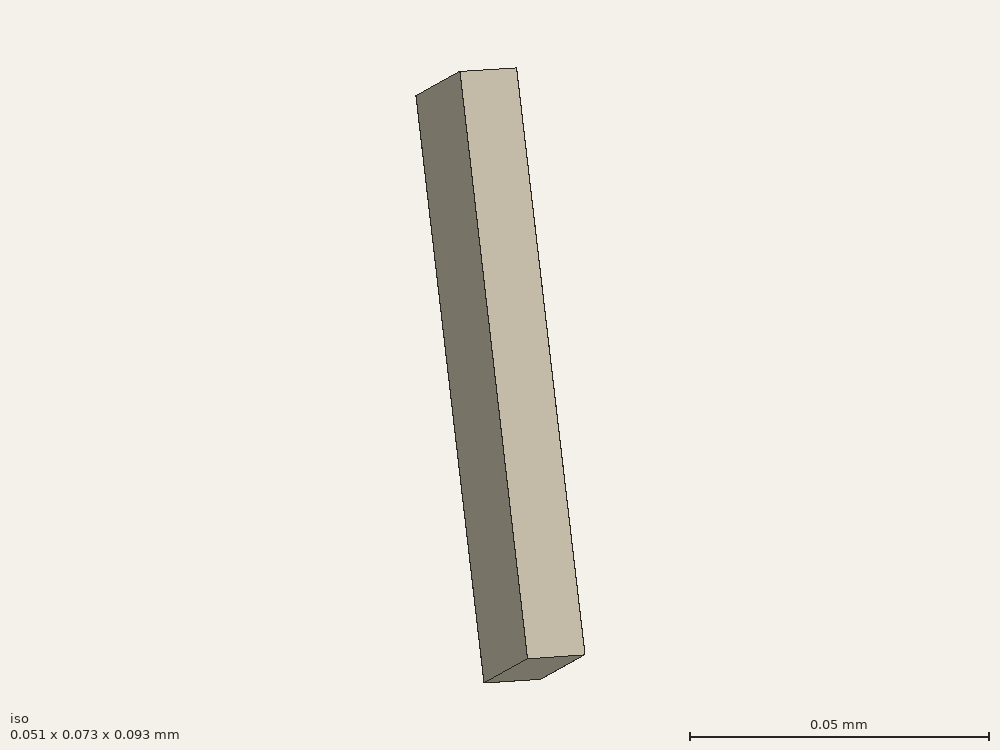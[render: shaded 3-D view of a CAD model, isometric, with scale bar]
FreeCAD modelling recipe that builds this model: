
FCSTD DOCUMENT  (FreeCAD 0.21R33694 (Git))
Label: straight-rotated
License: All rights reserved
LicenseURL: http://en.wikipedia.org/wiki/All_rights_reserved
objects: Part::Part2DObjectPython×5, App::FeaturePython×4, Part::Extrusion×1, Part::FeaturePython×1
note: 7 computed .brp shape members not serialized (recipe doc carries the construction recipe); baked Part::Feature solids carry a one-line shape summary decoded from their .brp

FEATURE [Part::Part2DObjectPython] Rectangle  # Draft 2D object (typed FeaturePython)
  Area = 232.258
  ChamferSize = 0
  Columns = 1
  FilletRadius = 0
  Height = 10.16
  Length = 22.86
  MakeFace = true
  Placement = pos=(-11.43,-5.08,0) rot=(0,0,1;0rad)
  Rows = 1
FEATURE [Part::Extrusion] Extrude
  Base = -> Rectangle
  Dir = (0,0,1)
  DirMode = 2
  FaceMakerClass = Part::FaceMakerBullseye
  LengthFwd = 100
  LengthRev = 0
  Solid = false
  Symmetric = false
FEATURE [Part::FeaturePython] Clone  label="Extrude001"  # Draft clone (typed FeaturePython)
  AttacherType = Attacher::AttachEngine3D
  Fuse = false
  Objects = -> [Extrude]
  Placement = pos=(-8.34567e-05,-0.00310102,-0.000489693) rot=(-0.540908,0.830402,-0.133611;3.77046rad)
  Scale = (0.001,0.001,0.001)
FEATURE [Part::Part2DObjectPython] Rectangle001  label="_Pport1"  # Draft 2D object (typed FeaturePython)
  Area = 0.000232258
  ChamferSize = 0
  Columns = 1
  FilletRadius = 0
  Height = 0.01016
  Length = 0.02286
  MakeFace = true
  Placement = pos=(-0.0281373,-0.0488265,-0.0858045) rot=(-0.540908,0.830402,-0.133611;3.77046rad)
  Rows = 1
FEATURE [Part::Part2DObjectPython] Line  label="_Pv1"  # Draft 2D object (typed FeaturePython)
  Area = 0
  ChamferSize = 0
  Closed = false
  End = (-0.0403847,-0.0527587,-0.0775334)
  FilletRadius = 0
  Length = 0.01016
  MakeFace = true
  Placement = pos=(-0.0313321,-0.0572141,-0.0787272) rot=(-0.540908,0.830402,-0.133611;3.77046rad)
  Points = (2) [(0,0,0),(-1.77605e-15,0.01016,0)]
  Start = (-0.0313321,-0.0572141,-0.0787272)
  Subdivisions = 0
FEATURE [Part::Part2DObjectPython] Rectangle002  label="_Pport2"  # Draft 2D object (typed FeaturePython)
  Area = 0.000232258
  ChamferSize = 0
  Columns = 1
  FilletRadius = 0
  Height = 0.01016
  Length = 0.02286
  MakeFace = true
  Placement = pos=(0.00763759,0.00305885,-0.00816386) rot=(-0.540908,0.830402,-0.133611;3.77046rad)
  Rows = 1
FEATURE [Part::Part2DObjectPython] Line001  label="_Pv2"  # Draft 2D object (typed FeaturePython)
  Area = 0
  ChamferSize = 0
  Closed = false
  End = (-0.00460977,-0.00087333,0.000107214)
  FilletRadius = 0
  Length = 0.01016
  MakeFace = true
  Placement = pos=(0.00444286,-0.0053287,-0.0010866) rot=(-0.540908,0.830402,-0.133611;3.77046rad)
  Points = (2) [(0,0,0),(3.1106e-19,0.01016,0)]
  Start = (0.00444286,-0.0053287,-0.0010866)
  Subdivisions = 0
FEATURE [App::FeaturePython] Text  label="_S1(PV){port1}"  # WARN: FeaturePython — macro-defined, semantics opaque (R4)
  Placement = pos=(0.0413747,-0.017509,0) rot=(0,0,1;0rad)
  Text = .
FEATURE [App::FeaturePython] Text001  label="_S2(PV){port2}"  # WARN: FeaturePython — macro-defined, semantics opaque (R4)
  Placement = pos=(0.0413747,-0.017509,0) rot=(0,0,1;0rad)
  Text = .
FEATURE [App::FeaturePython] Text002  label="_L1(1,voltage){v1}"  # WARN: FeaturePython — macro-defined, semantics opaque (R4)
  Placement = pos=(0.0413747,-0.017509,0) rot=(0,0,1;0rad)
  Text = .
FEATURE [App::FeaturePython] Text003  label="_L2(2,voltage){v2}"  # WARN: FeaturePython — macro-defined, semantics opaque (R4)
  Placement = pos=(0.0413747,-0.017509,0) rot=(0,0,1;0rad)
  Text = .
